# Revit family: 210_6fcddf30531344c3878c850dc72f7a
name_source: partatom
category: Duct Accessories
units: mm (PartAtom-declared; Revit-internal decimal feet)

## family parameters
Always vertical = Yes
Cut with Voids When Loaded = No
Part Type = Breaks Into
Round Connector Dimension = Use Diameter
Shared = No
Work Plane-Based = No

## types (6) — shared parameters
CAT0 = Yes
Description = IN LINE MIXED FLOW FAN - PP
LL = 5 mm  [stored 0.0164042 ft]
LL3 = 2 mm  [stored 0.00656168 ft]
LL__ve = -5 mm  [stored -0.0164042 ft]
Manufacturer = Alnor
QmdConnectorList = 201;D;202;D
URL = http://www.ventilation-alnor.co.uk
W = 500 mm
Z2 = 5 mm  [stored 0.0164042 ft]
magiPartTypeId = 210
magiProductFamilyId = 6fcddf30531344c3878c850dc72f7a

## per-type parameters (varying)
| type | BB2 | D | E | G | G__ve | LB2 | LL2 | LL4 | LM | LM2 | LM3 | LM3__ve | R | R1 | RH1 | WL | WL2 | YL | Z0 | Z1 | ZL | magiProductId |
| DV-PP-100-130 | 66 mm | 100 mm | 89 mm | 20 mm  [stored 0.0656168 ft] | -20 mm  [stored -0.0656168 ft] | 119 mm | 38 mm | 19 mm | 48 mm | 24 mm | 36 mm | -36 mm | 50 mm  [stored 0.164042 ft] | 28 mm | 19 mm | 100 mm | 50 mm  [stored 0.164042 ft] | 48 mm | 47 mm | 21 mm | 28 mm | bf73674e3cf14711bdfbc8606dc2e7 |
| DV-PP-200-910 | 104 mm | 200 mm | 140 mm | 52 mm | -52 mm | 177 mm | 86 mm | 43 mm | 71 mm | 35 mm | 59 mm | -59 mm | 100 mm | 55 mm | 31 mm | 142 mm | 71 mm | 95 mm | 74 mm | 44 mm | 55 mm | 32e0af3ec4d5464f9b97de646f03cf |
| DV-PP-160-560 | 92 mm | 160 mm | 115 mm | 21 mm | -21 mm | 157 mm | 39 mm | 20 mm  [stored 0.0656168 ft] | 63 mm | 31 mm | 51 mm | -51 mm | 80 mm | 44 mm | 27 mm | 130 mm | 65 mm | 76 mm | 65 mm | 44 mm | 44 mm | b9de3bd4137c426482943f9b5bd257 |
| DV-PP-150-560 | 92 mm | 150 mm | 115 mm | 21 mm | -21 mm | 147 mm | 39 mm | 20 mm  [stored 0.0656168 ft] | 59 mm | 29 mm | 47 mm | -47 mm | 75 mm | 41 mm | 27 mm | 130 mm | 65 mm | 71 mm | 65 mm | 44 mm | 41 mm | 4271e8086f214ccb8ed9e14e7de199 |
| DV-PP-125-320 | 81 mm | 125 mm | 100 mm | 21 mm | -21 mm | 131 mm | 39 mm | 20 mm  [stored 0.0656168 ft] | 52 mm | 26 mm | 40 mm | -40 mm | 63 mm | 34 mm | 24 mm | 100 mm | 50 mm  [stored 0.164042 ft] | 60 mm | 58 mm | 39 mm | 34 mm | 2768dd20c31345b19054315f204670 |
| DV-PP-100-270 | 86 mm | 100 mm | 115 mm | 20 mm  [stored 0.0656168 ft] | -20 mm  [stored -0.0656168 ft] | 155 mm | 38 mm | 19 mm | 62 mm | 31 mm | 50 mm  [stored 0.164042 ft] | -50 mm  [stored -0.164042 ft] | 50 mm  [stored 0.164042 ft] | 28 mm | 25 mm  [stored 0.082021 ft] | 130 mm | 65 mm | 48 mm | 61 mm | 34 mm | 28 mm | 8bb88241f06147c3b847a8d001d328 |

note: column(s) folded — value = type name in every type: MC Product Code

note: [stored X ft] marks values corroborated as IEEE doubles in the binary element streams (Revit-internal decimal feet)

## geometry (parser evidence)
native form markers: Blend x4, Sweep x2
no freeform markers — native parametric forms only
